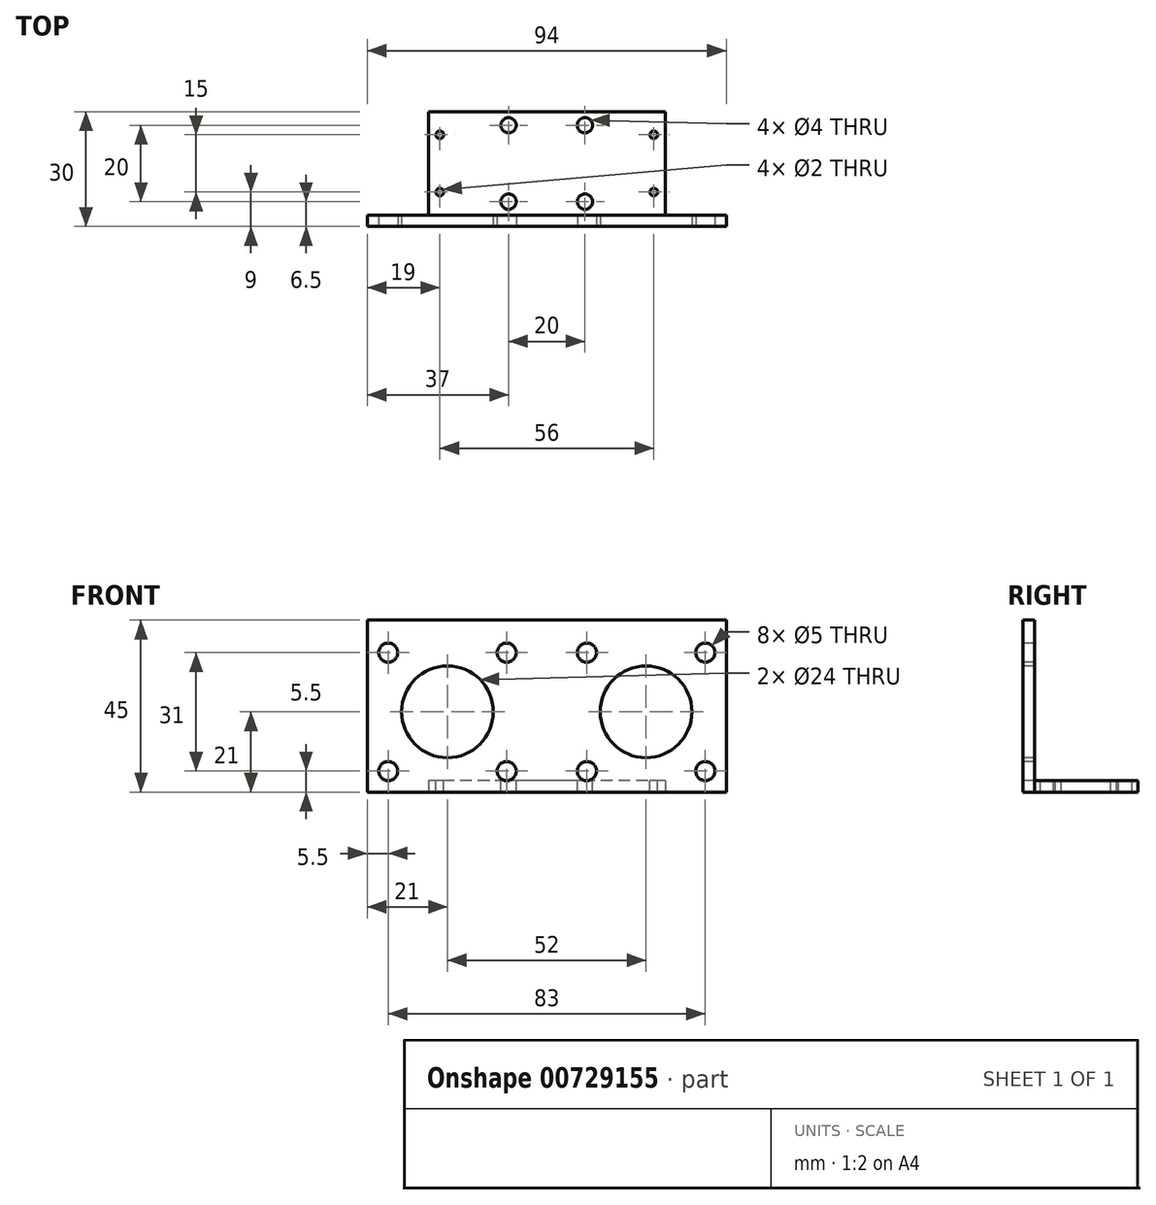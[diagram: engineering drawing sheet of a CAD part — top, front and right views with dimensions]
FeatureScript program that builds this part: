
annotation { "Feature Type Name" : "Feature", "Feature Type Description" : "" }
export const myFeature = defineFeature(function(context is Context, id is Id, definition is map)
    precondition{}
    {
        {
            var Q0;
            Q0=qCreatedBy(makeId("Top.planeOp"),FACE);
            var sketch = newSketch(context, id + "F0", { "sketchPlane" : qUnion([Q0])});
            skLineSegment(sketch, "E0.bottom", {"start": v(21, -15) * mm, "end": v(-21, -15) * mm});
            skLineSegment(sketch, "E0.top", {"start": v(21, 15) * mm, "end": v(-21, 15) * mm});
            skLineSegment(sketch, "E0.left", {"start": v(21, -15) * mm, "end": v(21, 15) * mm});
            skLineSegment(sketch, "E0.right", {"start": v(-21, -15) * mm, "end": v(-21, 15) * mm});
            skPoint(sketch, "E0.middle", {"position": v(0, 0) * mm});
            skLineSegment(sketch, "E1", {"start": v(21, -12) * mm, "end": v(-21, -12) * mm});
            skSolve(sketch);
        }
        {
            var Q0;
            {var subQ0=sQuery(id+"F0.wireOp",EDGE,"E0.top");Q0=makeQuery(id+"F0.imprint","IMPRINT",FACE,{"disambiguationData":[TD([[makeQuery(id+"F0.imprint","IMPRINT",EDGE,{"derivedFrom":subQ0}),1.0]])]});}
            extrude(context, id + "F1", {"entities" : qUnion([Q0]), "depth" : 3 * mm, "offsetDistance" : 25 * mm});
        }
        {
            var Q0;
            {var subQ0=sQuery(id+"F0.wireOp",EDGE,"E0.bottom");Q0=makeQuery(id+"F0.imprint","IMPRINT",FACE,{"disambiguationData":[TD([[makeQuery(id+"F0.imprint","IMPRINT",EDGE,{"derivedFrom":subQ0}),-1.0]])]});}
            extrude(context, id + "F2", {"entities" : qUnion([Q0]), "operationType" : NewBodyOperationType.ADD, "depth" : 45 * mm, "offsetDistance" : 25 * mm});
        }
        {
            var Q0;
            Q0=makeQuery(id+"F1.opExtrude","CAP_FACE",FACE,{"disambiguationData":[OSD([sQuery(id+"F0.wireOp",EDGE,"E0.top"),sQuery(id+"F0.wireOp",EDGE,"E0.left"),sQuery(id+"F0.wireOp",EDGE,"E0.right"),sQuery(id+"F0.wireOp",EDGE,"E1")])],"isStart":false});
            var sketch = newSketch(context, id + "F3", { "sketchPlane" : qUnion([Q0])});
            skLineSegment(sketch, "E2.bottom", {"start": v(10, -8.5) * mm, "end": v(-10, -8.5) * mm});
            skLineSegment(sketch, "E2.top", {"start": v(10, 11.5) * mm, "end": v(-10, 11.5) * mm});
            skLineSegment(sketch, "E2.left", {"start": v(10, -8.5) * mm, "end": v(10, 11.5) * mm});
            skLineSegment(sketch, "E2.right", {"start": v(-10, -8.5) * mm, "end": v(-10, 11.5) * mm});
            skSolve(sketch);
        }
        {
            var Q0;
            Q0=sQuery(id+"F3.wireOp",VERTEX,"E2.bottom.start");
            var Q1;
            Q1=sQuery(id+"F3.wireOp",VERTEX,"E2.left.end");
            var Q2;
            Q2=sQuery(id+"F3.wireOp",VERTEX,"E2.top.end");
            var Q3;
            Q3=sQuery(id+"F3.wireOp",VERTEX,"E2.right.start");
            var Q4;
            Q4=makeQuery(id+"F1.opExtrude","SWEPT_BODY",BODY,{"disambiguationData":[OSD([sQuery(id+"F0.wireOp",EDGE,"E0.top"),sQuery(id+"F0.wireOp",EDGE,"E0.left"),sQuery(id+"F0.wireOp",EDGE,"E0.right"),sQuery(id+"F0.wireOp",EDGE,"E1")])]});
            hole(context, id + "F4", {"style" : HoleStyle.SIMPLE, "endStyle" : HoleEndStyle.THROUGH, "holeDiameter" : 4 * mm, "majorDiameter" : 5 * mm, "isTappedThrough" : true, "tappedDepth" : 12 * mm, "tapClearance" : 3, "locations" : qUnion([Q0, Q1, Q2, Q3]), "scope" : qUnion([Q4])});
        }
        {
            var Q0;
            Q0=makeQuery(id+"F2.opExtrude","SWEPT_FACE",FACE,{"disambiguationData":[OSD([sQuery(id+"F0.wireOp",EDGE,"E1")])]});
            var sketch = newSketch(context, id + "F5", { "sketchPlane" : qUnion([Q0])});
            skLineSegment(sketch, "E3.bottom", {"start": v(15.5, 8.5) * mm, "end": v(-15.5, 8.5) * mm});
            skLineSegment(sketch, "E3.top", {"start": v(15.5, 39.5) * mm, "end": v(-15.5, 39.5) * mm});
            skLineSegment(sketch, "E3.left", {"start": v(15.5, 8.5) * mm, "end": v(15.5, 39.5) * mm});
            skLineSegment(sketch, "E3.right", {"start": v(-15.5, 8.5) * mm, "end": v(-15.5, 39.5) * mm});
            skPoint(sketch, "E3.middle", {"position": v(0, 24) * mm});
            skPoint(sketch, "E3.middle.positionSnap0", {"position": v(-21, 24) * mm});
            skPoint(sketch, "E3.centerSnap0", {"position": v(-21, 24) * mm});
            skSolve(sketch);
        }
        {
            var Q0;
            Q0=sQuery(id+"F5.wireOp",VERTEX,"E3.top.end");
            var Q1;
            Q1=sQuery(id+"F5.wireOp",VERTEX,"E3.bottom.end");
            var Q2;
            Q2=sQuery(id+"F5.wireOp",VERTEX,"E3.left.start");
            var Q3;
            Q3=sQuery(id+"F5.wireOp",VERTEX,"E3.top.start");
            var Q4;
            Q4=makeQuery(id+"F1.opExtrude","SWEPT_BODY",BODY,{"disambiguationData":[OSD([sQuery(id+"F0.wireOp",EDGE,"E0.top"),sQuery(id+"F0.wireOp",EDGE,"E0.left"),sQuery(id+"F0.wireOp",EDGE,"E0.right"),sQuery(id+"F0.wireOp",EDGE,"E1")])]});
            hole(context, id + "F6", {"style" : HoleStyle.SIMPLE, "endStyle" : HoleEndStyle.THROUGH, "holeDiameter" : 5 * mm, "majorDiameter" : 5 * mm, "isTappedThrough" : true, "tappedDepth" : 12 * mm, "tapClearance" : 3, "locations" : qUnion([Q0, Q1, Q2, Q3]), "scope" : qUnion([Q4])});
        }
        {
            var Q0;
            Q0=makeQuery(id+"F2.opExtrude","SWEPT_FACE",FACE,{"disambiguationData":[OSD([sQuery(id+"F0.wireOp",EDGE,"E1")])]});
            var sketch = newSketch(context, id + "F7", { "sketchPlane" : qUnion([Q0])});
            skCircle(sketch, "E4", {"center": v(0, 24) * mm, "radius": 12 * mm});
            skPoint(sketch, "E4.centerSnap0", {"position": v(0, 45) * mm});
            skPoint(sketch, "E4.centerSnap1", {"position": v(-21, 24) * mm});
            skSolve(sketch);
        }
        {
            var Q0;
            Q0=makeQuery(id+"F7.imprint","IMPRINT",FACE,{"disambiguationData":[TD([[makeQuery(id+"F7.imprint","IMPRINT",EDGE,{"derivedFrom":sQuery(id+"F7.wireOp",EDGE,"E4")}),1.0]])]});
            extrude(context, id + "F8", {"entities" : qUnion([Q0]), "operationType" : NewBodyOperationType.REMOVE, "oppositeDirection" : true, "depth" : 25 * mm, "offsetDistance" : 25 * mm});
        }
        {
            var Q0;
            {var subQ0=sQuery(id+"F0.wireOp",EDGE,"E0.right");Q0=makeQuery(id+"F2.boolean.opBoolean","MERGE",FACE,{"derivedFrom":[makeQuery(id+"F1.opExtrude","SWEPT_FACE",FACE,{"disambiguationData":[OSD([subQ0])]}),makeQuery(id+"F2.opExtrude","SWEPT_FACE",FACE,{"disambiguationData":[OSD([subQ0])]})]});}
            var sketch = newSketch(context, id + "F9", { "sketchPlane" : qUnion([Q0])});
            skPoint(sketch, "E5.oppositeSnap0", {"position": v(0, 0) * mm});
            skLineSegment(sketch, "E5.bottom", {"start": v(-15, 3) * mm, "end": v(12, 3) * mm});
            skLineSegment(sketch, "E5.top", {"start": v(-15, 0) * mm, "end": v(12, 0) * mm});
            skLineSegment(sketch, "E5.left", {"start": v(-15, 3) * mm, "end": v(-15, 0) * mm});
            skLineSegment(sketch, "E5.right", {"start": v(12, 3) * mm, "end": v(12, 0) * mm});
            skSolve(sketch);
        }
        {
            var Q0;
            Q0=makeQuery(id+"F9.imprint","IMPRINT",FACE,{"disambiguationData":[TD([[makeQuery(id+"F9.imprint","IMPRINT",EDGE,{"derivedFrom":sQuery(id+"F9.wireOp",EDGE,"E5.bottom")}),1.0]])]});
            extrude(context, id + "F10", {"entities" : qUnion([Q0]), "operationType" : NewBodyOperationType.ADD, "depth" : 10 * mm, "offsetDistance" : 25 * mm});
        }
        {
            var Q0;
            {var subQ0=sQuery(id+"F0.wireOp",EDGE,"E0.left");Q0=makeQuery(id+"F2.boolean.opBoolean","MERGE",FACE,{"derivedFrom":[makeQuery(id+"F1.opExtrude","SWEPT_FACE",FACE,{"disambiguationData":[OSD([subQ0])]}),makeQuery(id+"F2.opExtrude","SWEPT_FACE",FACE,{"disambiguationData":[OSD([subQ0])]})]});}
            var sketch = newSketch(context, id + "F11", { "sketchPlane" : qUnion([Q0])});
            skLineSegment(sketch, "E6.bottom", {"start": v(-12, 3) * mm, "end": v(15, 3) * mm});
            skLineSegment(sketch, "E6.top", {"start": v(-12, 0) * mm, "end": v(15, 0) * mm});
            skLineSegment(sketch, "E6.left", {"start": v(-12, 3) * mm, "end": v(-12, 0) * mm});
            skLineSegment(sketch, "E6.right", {"start": v(15, 3) * mm, "end": v(15, 0) * mm});
            skSolve(sketch);
        }
        {
            var Q0;
            Q0=qSketchRegion(id+"F11",true);
            extrude(context, id + "F12", {"entities" : qUnion([Q0]), "operationType" : NewBodyOperationType.ADD, "depth" : 10 * mm, "offsetDistance" : 25 * mm});
        }
        {
            var Q0;
            {var subQ0=sQuery(id+"F0.wireOp",EDGE,"E0.left");Q0=makeQuery(id+"F2.boolean.opBoolean","MERGE",FACE,{"derivedFrom":[makeQuery(id+"F1.opExtrude","SWEPT_FACE",FACE,{"disambiguationData":[OSD([subQ0])]}),makeQuery(id+"F2.opExtrude","SWEPT_FACE",FACE,{"disambiguationData":[OSD([subQ0])]})]});}
            var Q1;
            {var subQ0=sQuery(id+"F0.wireOp",EDGE,"E0.right");Q1=makeQuery(id+"F2.boolean.opBoolean","MERGE",FACE,{"derivedFrom":[makeQuery(id+"F1.opExtrude","SWEPT_FACE",FACE,{"disambiguationData":[OSD([subQ0])]}),makeQuery(id+"F2.opExtrude","SWEPT_FACE",FACE,{"disambiguationData":[OSD([subQ0])]})]});}
            extrude(context, id + "F13", {"entities" : qUnion([Q0, Q1]), "operationType" : NewBodyOperationType.ADD, "depth" : 26 * mm, "offsetDistance" : 25 * mm, "hasSecondDirection" : true, "secondDirectionOppositeDirection" : true, "secondDirectionDepth" : 26 * mm});
        }
        {
            var Q0;
            {var subQ0=sQuery(id+"F0.wireOp",EDGE,"E0.bottom");Q0=makeQuery(id+"F13.boolean.opBoolean","MERGE",FACE,{"derivedFrom":[makeQuery(id+"F2.opExtrude","SWEPT_FACE",FACE,{"disambiguationData":[OSD([subQ0])]}),makeQuery(id+"F13.opExtrude","SWEPT_FACE",FACE,{"disambiguationData":[OSD([subQ0,sQuery(id+"F0.wireOp",EDGE,"E0.left")])]}),makeQuery(id+"F13.opExtrude","SWEPT_FACE",FACE,{"disambiguationData":[OSD([subQ0,sQuery(id+"F0.wireOp",EDGE,"E0.right")])]})]});}
            var sketch = newSketch(context, id + "F14", { "sketchPlane" : qUnion([Q0])});
            skPoint(sketch, "E7", {"position": v(26, 21) * mm});
            skPoint(sketch, "E8", {"position": v(-26, 21) * mm});
            skLineSegment(sketch, "E9.bottom", {"start": v(10.5, 36.5) * mm, "end": v(41.5, 36.5) * mm});
            skLineSegment(sketch, "E9.top", {"start": v(10.5, 5.5) * mm, "end": v(41.5, 5.5) * mm});
            skLineSegment(sketch, "E9.left", {"start": v(10.5, 36.5) * mm, "end": v(10.5, 5.5) * mm});
            skLineSegment(sketch, "E9.right", {"start": v(41.5, 36.5) * mm, "end": v(41.5, 5.5) * mm});
            skLineSegment(sketch, "E10.bottom", {"start": v(-10.5, 5.5) * mm, "end": v(-41.5, 5.5) * mm});
            skLineSegment(sketch, "E10.top", {"start": v(-10.5, 36.5) * mm, "end": v(-41.5, 36.5) * mm});
            skLineSegment(sketch, "E10.left", {"start": v(-10.5, 5.5) * mm, "end": v(-10.5, 36.5) * mm});
            skLineSegment(sketch, "E10.right", {"start": v(-41.5, 5.5) * mm, "end": v(-41.5, 36.5) * mm});
            skCircle(sketch, "E11", {"center": v(-26, 21) * mm, "radius": 12 * mm});
            skCircle(sketch, "E12", {"center": v(26, 21) * mm, "radius": 12 * mm});
            skSolve(sketch);
        }
        {
            var Q0;
            Q0=makeQuery(id+"F14.imprint","IMPRINT",FACE,{"disambiguationData":[TD([[makeQuery(id+"F14.imprint","IMPRINT",EDGE,{"derivedFrom":sQuery(id+"F14.wireOp",EDGE,"E12")}),1.0]])]});
            var Q1;
            Q1=makeQuery(id+"F14.imprint","IMPRINT",FACE,{"disambiguationData":[TD([[makeQuery(id+"F14.imprint","IMPRINT",EDGE,{"derivedFrom":sQuery(id+"F14.wireOp",EDGE,"E11")}),1.0]])]});
            extrude(context, id + "F15", {"entities" : qUnion([Q0, Q1]), "operationType" : NewBodyOperationType.REMOVE, "oppositeDirection" : true, "depth" : 25 * mm, "offsetDistance" : 25 * mm});
        }
        {
            var Q0;
            Q0=sQuery(id+"F14.wireOp",VERTEX,"E9.right.end");
            var Q1;
            Q1=sQuery(id+"F14.wireOp",VERTEX,"E9.left.end");
            var Q2;
            Q2=sQuery(id+"F14.wireOp",VERTEX,"E9.bottom.end");
            var Q3;
            Q3=sQuery(id+"F14.wireOp",VERTEX,"E10.right.start");
            var Q4;
            Q4=sQuery(id+"F14.wireOp",VERTEX,"E10.bottom.start");
            var Q5;
            Q5=sQuery(id+"F14.wireOp",VERTEX,"E10.left.end");
            var Q6;
            Q6=sQuery(id+"F14.wireOp",VERTEX,"E10.right.end");
            var Q7;
            Q7=sQuery(id+"F14.wireOp",VERTEX,"E9.left.start");
            var Q8;
            Q8=makeQuery(id+"F1.opExtrude","SWEPT_BODY",BODY,{"disambiguationData":[OSD([sQuery(id+"F0.wireOp",EDGE,"E0.top"),sQuery(id+"F0.wireOp",EDGE,"E0.left"),sQuery(id+"F0.wireOp",EDGE,"E0.right"),sQuery(id+"F0.wireOp",EDGE,"E1")])]});
            hole(context, id + "F16", {"style" : HoleStyle.SIMPLE, "endStyle" : HoleEndStyle.THROUGH, "holeDiameter" : 5 * mm, "majorDiameter" : 5 * mm, "isTappedThrough" : true, "tappedDepth" : 12 * mm, "tapClearance" : 3, "locations" : qUnion([Q0, Q1, Q2, Q3, Q4, Q5, Q6, Q7]), "scope" : qUnion([Q8])});
        }
        {
            var Q0;
            Q0=makeQuery(id+"F12.boolean.opBoolean","MERGE",FACE,{"derivedFrom":[makeQuery(id+"F10.boolean.opBoolean","MERGE",FACE,{"derivedFrom":[makeQuery(id+"F1.opExtrude","CAP_FACE",FACE,{"disambiguationData":[OSD([sQuery(id+"F0.wireOp",EDGE,"E0.top"),sQuery(id+"F0.wireOp",EDGE,"E0.left"),sQuery(id+"F0.wireOp",EDGE,"E0.right"),sQuery(id+"F0.wireOp",EDGE,"E1")])],"isStart":false}),makeQuery(id+"F10.opExtrude","SWEPT_FACE",FACE,{"disambiguationData":[OSD([sQuery(id+"F9.wireOp",EDGE,"E5.bottom")])]})]}),makeQuery(id+"F12.opExtrude","SWEPT_FACE",FACE,{"disambiguationData":[OSD([sQuery(id+"F11.wireOp",EDGE,"E6.bottom")])]})]});
            var sketch = newSketch(context, id + "F17", { "sketchPlane" : qUnion([Q0])});
            skLineSegment(sketch, "E13.bottom", {"start": v(-28, 9) * mm, "end": v(28, 9) * mm});
            skLineSegment(sketch, "E13.top", {"start": v(-28, -6) * mm, "end": v(28, -6) * mm});
            skLineSegment(sketch, "E13.left", {"start": v(-28, 9) * mm, "end": v(-28, -6) * mm});
            skLineSegment(sketch, "E13.right", {"start": v(28, 9) * mm, "end": v(28, -6) * mm});
            skPoint(sketch, "E13.middle", {"position": v(0, 0) * mm});
            skSolve(sketch);
        }
        {
            var Q0;
            Q0=sQuery(id+"F17.wireOp",VERTEX,"E13.bottom.start");
            var Q1;
            Q1=sQuery(id+"F17.wireOp",VERTEX,"E13.left.end");
            var Q2;
            Q2=sQuery(id+"F17.wireOp",VERTEX,"E13.right.end");
            var Q3;
            Q3=sQuery(id+"F17.wireOp",VERTEX,"E13.bottom.end");
            var Q4;
            Q4=makeQuery(id+"F1.opExtrude","SWEPT_BODY",BODY,{"disambiguationData":[OSD([sQuery(id+"F0.wireOp",EDGE,"E0.top"),sQuery(id+"F0.wireOp",EDGE,"E0.left"),sQuery(id+"F0.wireOp",EDGE,"E0.right"),sQuery(id+"F0.wireOp",EDGE,"E1")])]});
            hole(context, id + "F18", {"style" : HoleStyle.SIMPLE, "endStyle" : HoleEndStyle.THROUGH, "holeDiameter" : 2 * mm, "majorDiameter" : 5 * mm, "isTappedThrough" : true, "tappedDepth" : 12 * mm, "tapClearance" : 3, "locations" : qUnion([Q0, Q1, Q2, Q3]), "scope" : qUnion([Q4])});
        }
    });
